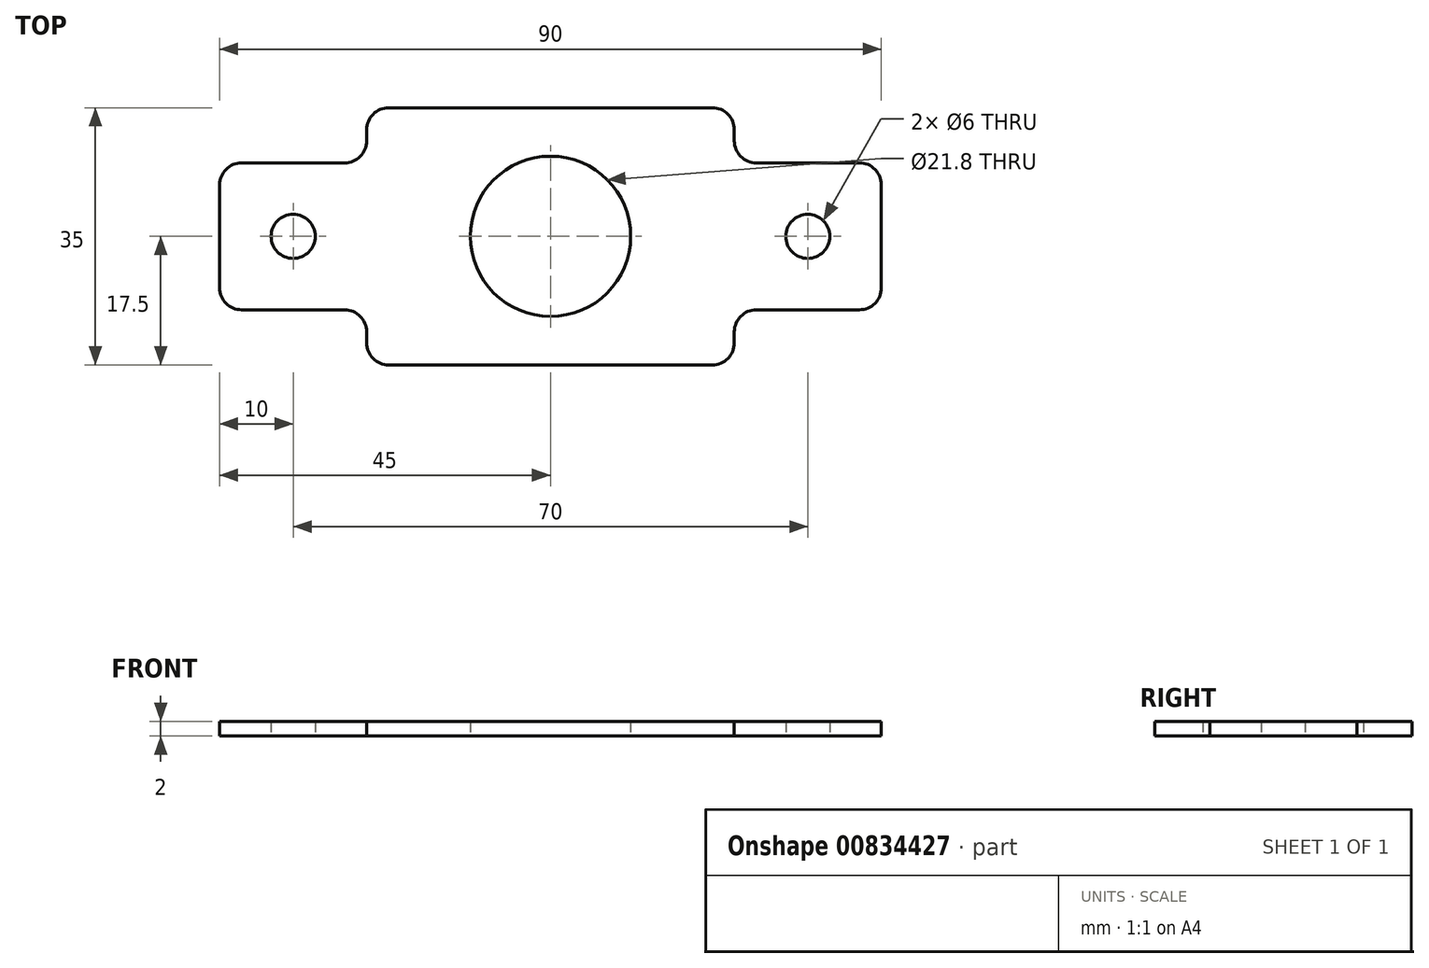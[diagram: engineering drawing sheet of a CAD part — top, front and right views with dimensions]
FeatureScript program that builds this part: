
annotation { "Feature Type Name" : "Feature", "Feature Type Description" : "" }
export const myFeature = defineFeature(function(context is Context, id is Id, definition is map)
    precondition{}
    {
        {
            var Q0;
            Q0=qCreatedBy(makeId("Top.planeOp"),FACE);
            var sketch = newSketch(context, id + "F0", { "sketchPlane" : qUnion([Q0])});
            skLineSegment(sketch, "E0.bottom", {"start": v(-25, 17.5) * mm, "end": v(25, 17.5) * mm});
            skLineSegment(sketch, "E0.top", {"start": v(-25, -17.5) * mm, "end": v(25, -17.5) * mm});
            skLineSegment(sketch, "E0.left", {"start": v(-25, 17.5) * mm, "end": v(-25, -17.5) * mm});
            skLineSegment(sketch, "E0.right", {"start": v(25, 17.5) * mm, "end": v(25, -17.5) * mm});
            skPoint(sketch, "E0.middle", {"position": v(0, 0) * mm});
            skLineSegment(sketch, "E1.bottom", {"start": v(-25, 10) * mm, "end": v(-45, 10) * mm});
            skLineSegment(sketch, "E1.top", {"start": v(-25, -10) * mm, "end": v(-45, -10) * mm});
            skLineSegment(sketch, "E1.left", {"start": v(-25, 10) * mm, "end": v(-25, -10) * mm});
            skLineSegment(sketch, "E1.right", {"start": v(-45, 10) * mm, "end": v(-45, -10) * mm});
            skLineSegment(sketch, "E2.MirrorCS", {"start": v(25, 10) * mm, "end": v(45, 10) * mm});
            skLineSegment(sketch, "E3.MirrorCS", {"start": v(45, 10) * mm, "end": v(45, -10) * mm});
            skLineSegment(sketch, "E4.MirrorCS", {"start": v(25, -10) * mm, "end": v(45, -10) * mm});
            skCircle(sketch, "E5", {"center": v(0, 0) * mm, "radius": 11.5 * mm});
            skCircle(sketch, "E6", {"center": v(0, 0) * mm, "radius": 10.9 * mm});
            skCircle(sketch, "E7", {"center": v(-35, 0) * mm, "radius": 3 * mm});
            skPoint(sketch, "E7.centerSnap0", {"position": v(-35, 10) * mm});
            skPoint(sketch, "E7.centerSnap1", {"position": v(-45, 0) * mm});
            skCircle(sketch, "E8.MirrorC", {"center": v(35, 0) * mm, "radius": 3 * mm});
            skSolve(sketch);
        }
        {
            var Q0;
            Q0=qSketchRegion(id+"F0",true);
            var Q1;
            Q1=makeQuery(id+"F0.imprint","IMPRINT",FACE,{"disambiguationData":[TD([[makeQuery(id+"F0.imprint","IMPRINT",EDGE,{"derivedFrom":sQuery(id+"F0.wireOp",EDGE,"E5")}),1.0]])]});
            extrude(context, id + "F1", {"entities" : qUnion([Q0, Q1]), "depth" : 2 * mm, "offsetDistance" : 25 * mm});
        }
        {
            var Q0;
            Q0=makeQuery(id+"F1.opExtrude","SWEPT_EDGE",EDGE,{"disambiguationData":[OSD([sQuery(id+"F0.wireOp",EDGE,"E0.left"),sQuery(id+"F0.wireOp",EDGE,"E1.top"),sQuery(id+"F0.wireOp",EDGE,"E1.left")])]});
            var Q1;
            Q1=makeQuery(id+"F1.opExtrude","SWEPT_EDGE",EDGE,{"disambiguationData":[OSD([sQuery(id+"F0.wireOp",EDGE,"E0.left"),sQuery(id+"F0.wireOp",EDGE,"E1.bottom"),sQuery(id+"F0.wireOp",EDGE,"E1.left")])]});
            var Q2;
            Q2=makeQuery(id+"F1.opExtrude","SWEPT_EDGE",EDGE,{"disambiguationData":[OSD([sQuery(id+"F0.wireOp",EDGE,"E0.right"),sQuery(id+"F0.wireOp",EDGE,"E2.MirrorCS")])]});
            var Q3;
            Q3=makeQuery(id+"F1.opExtrude","SWEPT_EDGE",EDGE,{"disambiguationData":[OSD([sQuery(id+"F0.wireOp",EDGE,"E0.right"),sQuery(id+"F0.wireOp",EDGE,"E4.MirrorCS")])]});
            var Q4;
            Q4=makeQuery(id+"F1.opExtrude","SWEPT_EDGE",EDGE,{"disambiguationData":[OSD([sQuery(id+"F0.wireOp",EDGE,"E0.bottom"),sQuery(id+"F0.wireOp",EDGE,"E0.right")])]});
            var Q5;
            Q5=makeQuery(id+"F1.opExtrude","SWEPT_EDGE",EDGE,{"disambiguationData":[OSD([sQuery(id+"F0.wireOp",EDGE,"E0.top"),sQuery(id+"F0.wireOp",EDGE,"E0.right")])]});
            var Q6;
            Q6=makeQuery(id+"F1.opExtrude","SWEPT_EDGE",EDGE,{"disambiguationData":[OSD([sQuery(id+"F0.wireOp",EDGE,"E0.top"),sQuery(id+"F0.wireOp",EDGE,"E0.left")])]});
            var Q7;
            Q7=makeQuery(id+"F1.opExtrude","SWEPT_EDGE",EDGE,{"disambiguationData":[OSD([sQuery(id+"F0.wireOp",EDGE,"E0.bottom"),sQuery(id+"F0.wireOp",EDGE,"E0.left")])]});
            var Q8;
            Q8=makeQuery(id+"F1.opExtrude","SWEPT_EDGE",EDGE,{"disambiguationData":[OSD([sQuery(id+"F0.wireOp",EDGE,"E1.bottom"),sQuery(id+"F0.wireOp",EDGE,"E1.right")])]});
            var Q9;
            Q9=makeQuery(id+"F1.opExtrude","SWEPT_EDGE",EDGE,{"disambiguationData":[OSD([sQuery(id+"F0.wireOp",EDGE,"E1.top"),sQuery(id+"F0.wireOp",EDGE,"E1.right")])]});
            var Q10;
            Q10=makeQuery(id+"F1.opExtrude","SWEPT_EDGE",EDGE,{"disambiguationData":[OSD([sQuery(id+"F0.wireOp",EDGE,"E3.MirrorCS"),sQuery(id+"F0.wireOp",EDGE,"E4.MirrorCS")])]});
            var Q11;
            Q11=makeQuery(id+"F1.opExtrude","SWEPT_EDGE",EDGE,{"disambiguationData":[OSD([sQuery(id+"F0.wireOp",EDGE,"E2.MirrorCS"),sQuery(id+"F0.wireOp",EDGE,"E3.MirrorCS")])]});
            fillet(context, id + "F2", {"entities" : qUnion([Q0, Q1, Q2, Q3, Q4, Q5, Q6, Q7, Q8, Q9, Q10, Q11]), "radius" : 3 * mm, "tangentPropagation" : true, "allowEdgeOverflow" : false});
        }
    });
